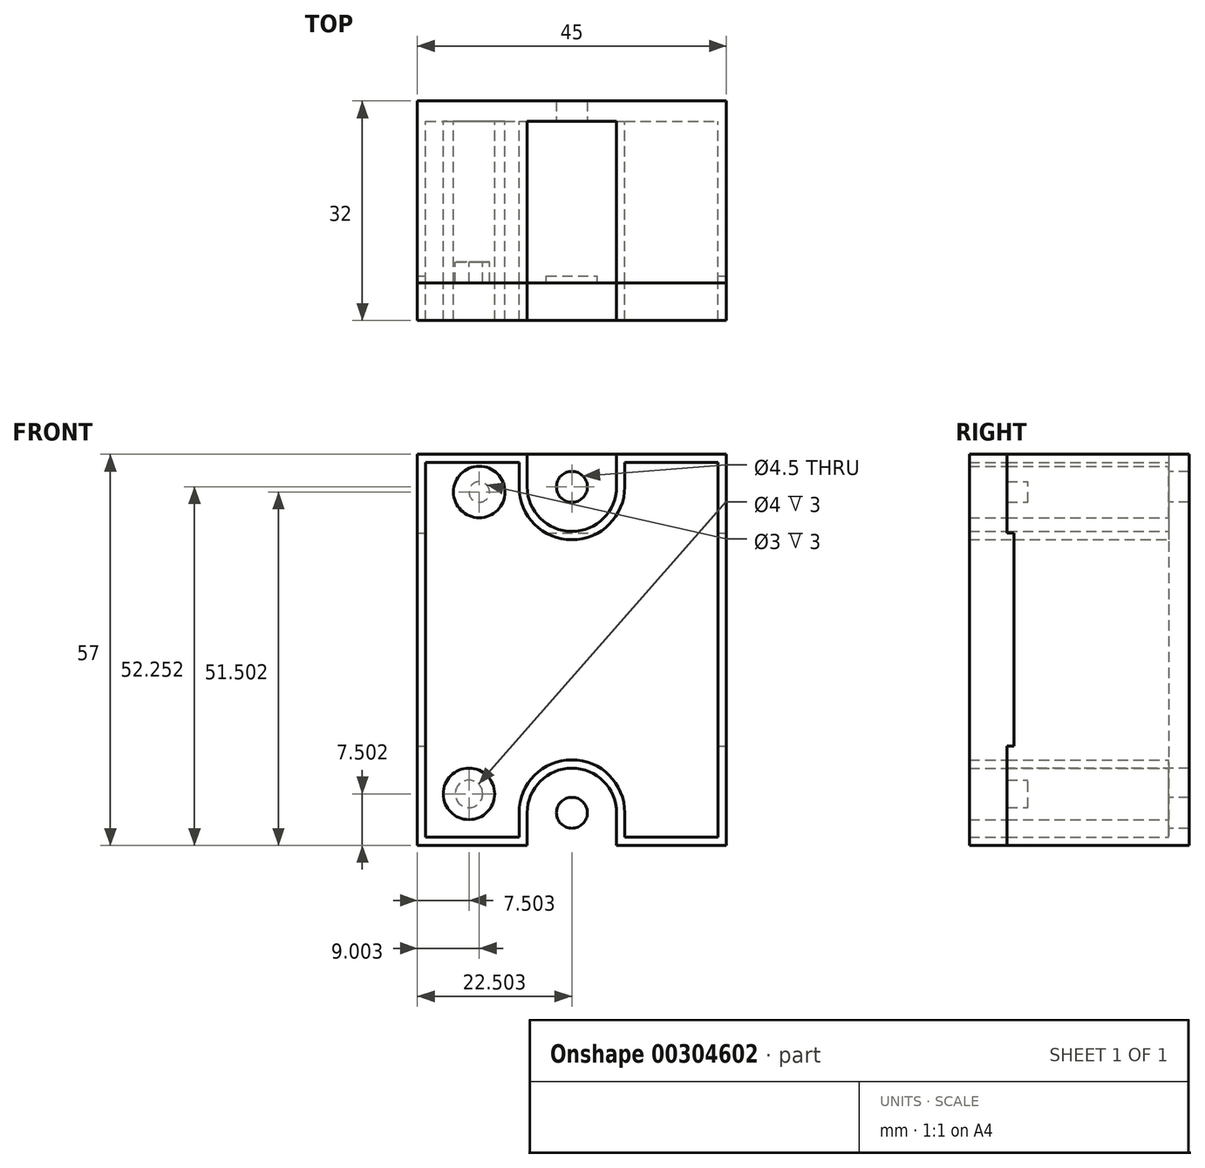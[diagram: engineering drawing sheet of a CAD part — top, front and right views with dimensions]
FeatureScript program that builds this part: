
annotation { "Feature Type Name" : "Feature", "Feature Type Description" : "" }
export const myFeature = defineFeature(function(context is Context, id is Id, definition is map)
    precondition{}
    {
        {
            var Q0;
            Q0=qCreatedBy(makeId("Front.planeOp"),FACE);
            var sketch = newSketch(context, id + "F0", { "sketchPlane" : qUnion([Q0])});
            skLineSegment(sketch, "E0.bottom", {"start": v(-24.48, 28.44) * mm, "end": v(20.52, 28.44) * mm});
            skLineSegment(sketch, "E0.top", {"start": v(-24.48, -28.56) * mm, "end": v(20.52, -28.56) * mm});
            skLineSegment(sketch, "E0.left", {"start": v(-24.48, 28.44) * mm, "end": v(-24.48, -28.56) * mm});
            skLineSegment(sketch, "E0.right", {"start": v(20.52, 28.44) * mm, "end": v(20.52, -28.56) * mm});
            skLineSegment(sketch, "E1", {"start": v(-1.98, 28.44) * mm, "end": v(-1.98, -28.56) * mm, "construction": true});
            skLineSegment(sketch, "E2", {"start": v(-24.48, -0.06) * mm, "end": v(20.52, -0.06) * mm, "construction": true});
            skCircle(sketch, "E3", {"center": v(-1.98, 23.7) * mm, "radius": 2.25 * mm});
            skCircle(sketch, "E4.MirrorC", {"center": v(-1.98, -23.8) * mm, "radius": 2.25 * mm});
            skLineSegment(sketch, "E5", {"start": v(-33.93, 23.7) * mm, "end": v(32.5, 23.7) * mm, "construction": true});
            skLineSegment(sketch, "E6", {"start": v(4.52, 28.44) * mm, "end": v(4.52, 23.7) * mm});
            skLineSegment(sketch, "E7.MirrorCS", {"start": v(-8.48, 28.44) * mm, "end": v(-8.48, 23.7) * mm});
            skArc(sketch, "E8", {"start": v(-8.48, 23.7) * mm, "mid": v(-1.98, 17.2) * mm, "end": v(4.52, 23.7) * mm});
            skLineSegment(sketch, "E9", {"start": v(-24.48, 17.2) * mm, "end": v(20.52, 17.2) * mm, "construction": true});
            skArc(sketch, "E10.MirrorCS", {"start": v(-8.48, -23.8) * mm, "mid": v(-1.98, -17.3) * mm, "end": v(4.52, -23.8) * mm});
            skLineSegment(sketch, "E11.MirrorCS", {"start": v(-8.48, -28.56) * mm, "end": v(-8.48, -23.8) * mm});
            skLineSegment(sketch, "E12.MirrorCS", {"start": v(4.52, -28.56) * mm, "end": v(4.52, -23.8) * mm});
            skSolve(sketch);
        }
        {
            var Q0;
            {var subQ2=sQuery(id+"F0.wireOp",EDGE,"E0.left");Q0=makeQuery(id+"F0.imprint","IMPRINT",FACE,{"disambiguationData":[TD([[makeQuery(id+"F0.imprint","IMPRINT",EDGE,{"derivedFrom":subQ2}),1.0]])]});}
            var Q1;
            Q1=makeQuery(id+"F0.imprint","IMPRINT",FACE,{"disambiguationData":[TD([[makeQuery(id+"F0.imprint","IMPRINT",EDGE,{"derivedFrom":sQuery(id+"F0.wireOp",EDGE,"E3")}),-1.0]])]});
            var Q2;
            Q2=makeQuery(id+"F0.imprint","IMPRINT",FACE,{"disambiguationData":[TD([[makeQuery(id+"F0.imprint","IMPRINT",EDGE,{"derivedFrom":sQuery(id+"F0.wireOp",EDGE,"E4.MirrorC")}),1.0]])]});
            extrude(context, id + "F1", {"entities" : qUnion([Q0, Q1, Q2]), "oppositeDirection" : true, "depth" : 3 * mm});
        }
        {
            var Q0;
            {var subQ2=sQuery(id+"F0.wireOp",EDGE,"E0.left");Q0=makeQuery(id+"F0.imprint","IMPRINT",FACE,{"disambiguationData":[TD([[makeQuery(id+"F0.imprint","IMPRINT",EDGE,{"derivedFrom":subQ2}),1.0]])]});}
            extrude(context, id + "F2", {"entities" : qUnion([Q0]), "operationType" : NewBodyOperationType.ADD, "depth" : 20.5 * mm});
        }
        {
            var Q0;
            Q0=makeQuery(id+"F2.opExtrude","CAP_FACE",FACE,{"disambiguationData":[OSD([sQuery(id+"F0.wireOp",EDGE,"E0.bottom"),sQuery(id+"F0.wireOp",EDGE,"E0.top"),sQuery(id+"F0.wireOp",EDGE,"E0.left"),sQuery(id+"F0.wireOp",EDGE,"E0.right"),sQuery(id+"F0.wireOp",EDGE,"E6"),sQuery(id+"F0.wireOp",EDGE,"E7.MirrorCS"),sQuery(id+"F0.wireOp",EDGE,"E8"),sQuery(id+"F0.wireOp",EDGE,"E10.MirrorCS"),sQuery(id+"F0.wireOp",EDGE,"E11.MirrorCS"),sQuery(id+"F0.wireOp",EDGE,"E12.MirrorCS")])],"isStart":false});
            var sketch = newSketch(context, id + "F3", { "sketchPlane" : qUnion([Q0])});
            skLineSegment(sketch, "E13.0", {"start": v(-24.48, -0.06) * mm, "end": v(20.52, -0.06) * mm, "construction": true});
            skLineSegment(sketch, "E14.bottom", {"start": v(-24.48, -14.06) * mm, "end": v(20.52, -14.06) * mm});
            skLineSegment(sketch, "E14.top", {"start": v(-24.48, 16.94) * mm, "end": v(20.52, 16.94) * mm});
            skLineSegment(sketch, "E14.left", {"start": v(-24.48, -14.06) * mm, "end": v(-24.48, 16.94) * mm});
            skLineSegment(sketch, "E14.right", {"start": v(20.52, -14.06) * mm, "end": v(20.52, 16.94) * mm});
            skCircle(sketch, "E15", {"center": v(-16.98, -21.06) * mm, "radius": 4.75 * mm});
            skCircle(sketch, "E16", {"center": v(-16.98, -21.06) * mm, "radius": 2 * mm});
            skCircle(sketch, "E17", {"center": v(-15.48, 22.94) * mm, "radius": 3.5 * mm});
            skCircle(sketch, "E18", {"center": v(-15.48, 22.94) * mm, "radius": 1.5 * mm});
            skCircle(sketch, "E19.MirrorC", {"center": v(13.02, -21.06) * mm, "radius": 4.75 * mm});
            skCircle(sketch, "E20.MirrorC", {"center": v(13.02, -21.06) * mm, "radius": 2 * mm});
            skCircle(sketch, "E21.MirrorC", {"center": v(11.52, 22.94) * mm, "radius": 3.5 * mm});
            skCircle(sketch, "E22.MirrorC", {"center": v(11.52, 22.94) * mm, "radius": 1.5 * mm});
            skSolve(sketch);
        }
        {
            var Q0;
            Q0=makeQuery(id+"F3.imprint","IMPRINT",FACE,{"disambiguationData":[TD([[makeQuery(id+"F3.imprint","IMPRINT",EDGE,{"derivedFrom":sQuery(id+"F3.wireOp",EDGE,"E14.bottom")}),1.0]])]});
            extrude(context, id + "F4", {"entities" : qUnion([Q0]), "operationType" : NewBodyOperationType.ADD, "depth" : 2 * mm});
        }
        {
            var Q0;
            Q0=makeQuery(id+"F3.imprint","IMPRINT",FACE,{"disambiguationData":[TD([[makeQuery(id+"F3.imprint","IMPRINT",EDGE,{"derivedFrom":sQuery(id+"F3.wireOp",EDGE,"E15")}),1.0]])]});
            var Q1;
            Q1=makeQuery(id+"F3.imprint","IMPRINT",FACE,{"disambiguationData":[TD([[makeQuery(id+"F3.imprint","IMPRINT",EDGE,{"derivedFrom":sQuery(id+"F3.wireOp",EDGE,"E17")}),1.0]])]});
            var Q2;
            Q2=makeQuery(id+"F3.imprint","IMPRINT",FACE,{"disambiguationData":[TD([[makeQuery(id+"F3.imprint","IMPRINT",EDGE,{"derivedFrom":sQuery(id+"F3.wireOp",EDGE,"E21.MirrorC")}),-1.0]])]});
            var Q3;
            Q3=makeQuery(id+"F3.imprint","IMPRINT",FACE,{"disambiguationData":[TD([[makeQuery(id+"F3.imprint","IMPRINT",EDGE,{"derivedFrom":sQuery(id+"F3.wireOp",EDGE,"E19.MirrorC")}),-1.0]])]});
            extrude(context, id + "F5", {"entities" : qUnion([Q0, Q1, Q2, Q3]), "operationType" : NewBodyOperationType.ADD, "depth" : 3 * mm});
        }
        {
            var Q0;
            {var subQ2=sQuery(id+"F0.wireOp",EDGE,"E0.left");Q0=makeQuery(id+"F0.imprint","IMPRINT",FACE,{"disambiguationData":[TD([[makeQuery(id+"F0.imprint","IMPRINT",EDGE,{"derivedFrom":subQ2}),1.0]])]});}
            var Q1;
            Q1=makeQuery(id+"F1.opExtrude","SWEPT_BODY",BODY,{"disambiguationData":[OSD([sQuery(id+"F0.wireOp",EDGE,"E0.bottom"),sQuery(id+"F0.wireOp",EDGE,"E0.top"),sQuery(id+"F0.wireOp",EDGE,"E0.left"),sQuery(id+"F0.wireOp",EDGE,"E0.right"),sQuery(id+"F0.wireOp",EDGE,"E3"),sQuery(id+"F0.wireOp",EDGE,"E4.MirrorC")])]});
            extrude(context, id + "F6", {"entities" : qUnion([Q0]), "depth" : 29 * mm, "hasSecondDirection" : true, "secondDirectionBound" : SecondDirectionBoundingType.UP_TO_BODY, "secondDirectionOppositeDirection" : false, "secondDirectionBoundEntityBody" : qUnion([Q1]), "secondDirectionDepth" : 25 * mm});
        }
        {
            var Q0;
            {var subQ2=sQuery(id+"F0.wireOp",EDGE,"E0.left");Q0=makeQuery(id+"F0.imprint","IMPRINT",FACE,{"disambiguationData":[TD([[makeQuery(id+"F0.imprint","IMPRINT",EDGE,{"derivedFrom":subQ2}),1.0]])]});}
            var sketch = newSketch(context, id + "F7", { "sketchPlane" : qUnion([Q0])});
            skCircle(sketch, "E23", {"center": v(11.52, 22.94) * mm, "radius": 3.75 * mm});
            skPoint(sketch, "E24.0", {"position": v(13.02, -21.06) * mm});
            skCircle(sketch, "E25", {"center": v(13.02, -21.06) * mm, "radius": 3.75 * mm});
            skCircle(sketch, "E26.MirrorC", {"center": v(-15.48, 22.94) * mm, "radius": 3.75 * mm});
            skCircle(sketch, "E27.MirrorC", {"center": v(-16.98, -21.06) * mm, "radius": 3.75 * mm});
            skLineSegment(sketch, "E28.0", {"start": v(4.52, 28.44) * mm, "end": v(20.52, 28.44) * mm, "construction": true});
            skLineSegment(sketch, "E29.0", {"start": v(20.52, 28.44) * mm, "end": v(20.52, 16.94) * mm, "construction": true});
            skLineSegment(sketch, "E30.0", {"start": v(20.52, 16.94) * mm, "end": v(20.52, -14.06) * mm, "construction": true});
            skLineSegment(sketch, "E31.0", {"start": v(20.52, -14.06) * mm, "end": v(20.52, -28.56) * mm, "construction": true});
            skLineSegment(sketch, "E32.0", {"start": v(4.52, -28.56) * mm, "end": v(20.52, -28.56) * mm, "construction": true});
            skArc(sketch, "E33.0", {"start": v(-8.48, -23.8) * mm, "mid": v(-1.98, -17.3) * mm, "end": v(4.52, -23.8) * mm, "construction": true});
            skLineSegment(sketch, "E34.0", {"start": v(4.52, -28.56) * mm, "end": v(4.52, -23.8) * mm, "construction": true});
            skLineSegment(sketch, "E35.0", {"start": v(-8.48, -28.56) * mm, "end": v(-8.48, -23.8) * mm, "construction": true});
            skLineSegment(sketch, "E36.0", {"start": v(-24.48, -28.56) * mm, "end": v(-8.48, -28.56) * mm, "construction": true});
            skLineSegment(sketch, "E37.0", {"start": v(-24.48, -14.06) * mm, "end": v(-24.48, -28.56) * mm, "construction": true});
            skLineSegment(sketch, "E38.0", {"start": v(-24.48, 16.94) * mm, "end": v(-24.48, -14.06) * mm, "construction": true});
            skLineSegment(sketch, "E39.0", {"start": v(-24.48, 28.44) * mm, "end": v(-24.48, 16.94) * mm, "construction": true});
            skLineSegment(sketch, "E40.0", {"start": v(-24.48, 28.44) * mm, "end": v(-8.48, 28.44) * mm, "construction": true});
            skArc(sketch, "E41.0", {"start": v(-8.48, 23.7) * mm, "mid": v(-1.98, 17.2) * mm, "end": v(4.52, 23.7) * mm, "construction": true});
            skLineSegment(sketch, "E42.0", {"start": v(-8.48, 28.44) * mm, "end": v(-8.48, 23.7) * mm, "construction": true});
            skLineSegment(sketch, "E43.0", {"start": v(4.52, 28.44) * mm, "end": v(4.52, 23.7) * mm, "construction": true});
            skLineSegment(sketch, "E44.0", {"start": v(5.72, 27.24) * mm, "end": v(5.72, 23.7) * mm});
            skArc(sketch, "E44.1", {"start": v(-9.68, 23.7) * mm, "mid": v(-1.98, 16) * mm, "end": v(5.72, 23.7) * mm});
            skLineSegment(sketch, "E44.2", {"start": v(-9.68, 27.24) * mm, "end": v(-9.68, 23.7) * mm});
            skLineSegment(sketch, "E44.3", {"start": v(-23.28, 27.24) * mm, "end": v(-9.68, 27.24) * mm});
            skLineSegment(sketch, "E44.4", {"start": v(-23.28, 27.24) * mm, "end": v(-23.28, 16.94) * mm});
            skLineSegment(sketch, "E44.5", {"start": v(5.72, -27.36) * mm, "end": v(19.32, -27.36) * mm});
            skLineSegment(sketch, "E44.6", {"start": v(19.32, -14.06) * mm, "end": v(19.32, -27.36) * mm});
            skLineSegment(sketch, "E44.7", {"start": v(19.32, 16.94) * mm, "end": v(19.32, -14.06) * mm});
            skLineSegment(sketch, "E44.8", {"start": v(19.32, 27.24) * mm, "end": v(19.32, 16.94) * mm});
            skLineSegment(sketch, "E44.9", {"start": v(5.72, -27.36) * mm, "end": v(5.72, -23.8) * mm});
            skArc(sketch, "E44.10", {"start": v(-9.68, -23.8) * mm, "mid": v(-1.98, -16.1) * mm, "end": v(5.72, -23.8) * mm});
            skLineSegment(sketch, "E44.11", {"start": v(-9.68, -27.36) * mm, "end": v(-9.68, -23.8) * mm});
            skLineSegment(sketch, "E44.12", {"start": v(-23.28, -27.36) * mm, "end": v(-9.68, -27.36) * mm});
            skLineSegment(sketch, "E44.13", {"start": v(-23.28, -14.06) * mm, "end": v(-23.28, -27.36) * mm});
            skLineSegment(sketch, "E44.14", {"start": v(5.72, 27.24) * mm, "end": v(19.32, 27.24) * mm});
            skLineSegment(sketch, "E44.15", {"start": v(-23.28, 16.94) * mm, "end": v(-23.28, -14.06) * mm});
            skSolve(sketch);
        }
        {
            var Q0;
            Q0=makeQuery(id+"F7.imprint","IMPRINT",FACE,{"disambiguationData":[TD([[makeQuery(id+"F7.imprint","IMPRINT",EDGE,{"derivedFrom":sQuery(id+"F7.wireOp",EDGE,"E23")}),1.0]])]});
            var Q1;
            Q1=makeQuery(id+"F7.imprint","IMPRINT",FACE,{"disambiguationData":[TD([[makeQuery(id+"F7.imprint","IMPRINT",EDGE,{"derivedFrom":sQuery(id+"F7.wireOp",EDGE,"E26.MirrorC")}),-1.0]])]});
            var Q2;
            Q2=makeQuery(id+"F7.imprint","IMPRINT",FACE,{"disambiguationData":[TD([[makeQuery(id+"F7.imprint","IMPRINT",EDGE,{"derivedFrom":sQuery(id+"F7.wireOp",EDGE,"E27.MirrorC")}),-1.0]])]});
            var Q3;
            Q3=makeQuery(id+"F7.imprint","IMPRINT",FACE,{"disambiguationData":[TD([[makeQuery(id+"F7.imprint","IMPRINT",EDGE,{"derivedFrom":sQuery(id+"F7.wireOp",EDGE,"E25")}),1.0]])]});
            extrude(context, id + "F8", {"entities" : qUnion([Q0, Q1, Q2, Q3]), "operationType" : NewBodyOperationType.REMOVE, "depth" : 48.3 * mm});
        }
        {
            var Q0;
            Q0=makeQuery(id+"F7.imprint","IMPRINT",FACE,{"disambiguationData":[TD([[makeQuery(id+"F7.imprint","IMPRINT",EDGE,{"derivedFrom":sQuery(id+"F7.wireOp",EDGE,"E23")}),-1.0]])]});
            var Q1;
            Q1=makeQuery(id+"F7.imprint","IMPRINT",FACE,{"disambiguationData":[TD([[makeQuery(id+"F7.imprint","IMPRINT",EDGE,{"derivedFrom":sQuery(id+"F7.wireOp",EDGE,"E23")}),1.0]])]});
            var Q2;
            Q2=makeQuery(id+"F7.imprint","IMPRINT",FACE,{"disambiguationData":[TD([[makeQuery(id+"F7.imprint","IMPRINT",EDGE,{"derivedFrom":sQuery(id+"F7.wireOp",EDGE,"E26.MirrorC")}),-1.0]])]});
            var Q3;
            Q3=makeQuery(id+"F7.imprint","IMPRINT",FACE,{"disambiguationData":[TD([[makeQuery(id+"F7.imprint","IMPRINT",EDGE,{"derivedFrom":sQuery(id+"F7.wireOp",EDGE,"E27.MirrorC")}),-1.0]])]});
            var Q4;
            Q4=makeQuery(id+"F7.imprint","IMPRINT",FACE,{"disambiguationData":[TD([[makeQuery(id+"F7.imprint","IMPRINT",EDGE,{"derivedFrom":sQuery(id+"F7.wireOp",EDGE,"E25")}),1.0]])]});
            extrude(context, id + "F9", {"entities" : qUnion([Q0, Q1, Q2, Q3, Q4]), "operationType" : NewBodyOperationType.REMOVE, "depth" : 27.5 * mm});
        }
    });
